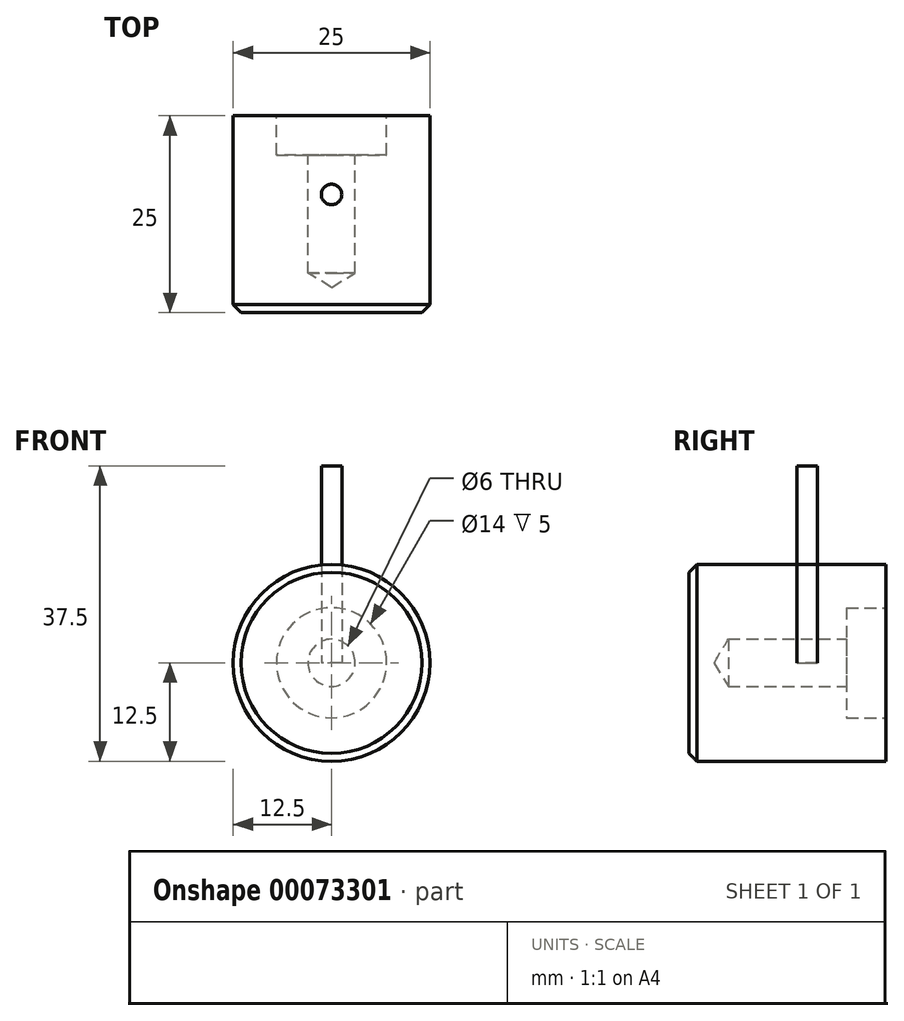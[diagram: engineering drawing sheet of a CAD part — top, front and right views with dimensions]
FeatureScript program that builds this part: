
annotation { "Feature Type Name" : "Feature", "Feature Type Description" : "" }
export const myFeature = defineFeature(function(context is Context, id is Id, definition is map)
    precondition{}
    {
        {
            var Q0;
            Q0=qCreatedBy(makeId("Front.planeOp"),FACE);
            var sketch = newSketch(context, id + "F0", { "sketchPlane" : qUnion([Q0])});
            skCircle(sketch, "E0", {"center": v(0, 0) * mm, "radius": 12.5 * mm});
            skSolve(sketch);
        }
        {
            var Q0;
            Q0=qSketchRegion(id+"F0",true);
            var Q1;
            Q1=makeQuery(id+"F0.imprint","IMPRINT",FACE,{"disambiguationData":[TD([[makeQuery(id+"F0.imprint","IMPRINT",EDGE,{"derivedFrom":sQuery(id+"F0.wireOp",EDGE,"E0")}),1.0]])]});
            extrude(context, id + "F1", {"entities" : qUnion([Q0, Q1]), "depth" : 25 * mm});
        }
        {
            var Q0;
            Q0=makeQuery(id+"F1.opExtrude","CAP_EDGE",EDGE,{"disambiguationData":[OSD([sQuery(id+"F0.wireOp",EDGE,"E0")])],"isStart":false});
            chamfer(context, id + "F2", {"entities" : qUnion([Q0]), "width" : 1 * mm, "tangentPropagation" : true});
        }
        {
            var Q0;
            Q0=makeQuery(id+"F1.opExtrude","CAP_FACE",FACE,{"disambiguationData":[OSD([sQuery(id+"F0.wireOp",EDGE,"E0")])],"isStart":true});
            var sketch = newSketch(context, id + "F3", { "sketchPlane" : qUnion([Q0])});
            skPoint(sketch, "E1", {"position": v(0, 0) * mm});
            skSolve(sketch);
        }
        {
            var Q0;
            Q0=sQuery(id+"F3.wireOp",VERTEX,"E1");
            var Q1;
            Q1=makeQuery(id+"F1.opExtrude","SWEPT_BODY",BODY,{"disambiguationData":[OSD([sQuery(id+"F0.wireOp",EDGE,"E0")])]});
            hole(context, id + "F4", {"style" : HoleStyle.C_BORE, "holeDiameter" : 6 * mm, "cBoreDiameter" : 14 * mm, "cBoreDepth" : 5 * mm, "endStyle" : HoleEndStyle.BLIND, "holeDepth" : 20 * mm, "locations" : qUnion([Q0]), "scope" : qUnion([Q1])});
        }
        {
            var Q0;
            Q0=qCreatedBy(makeId("Top.planeOp"),FACE);
            var sketch = newSketch(context, id + "F5", { "sketchPlane" : qUnion([Q0])});
            skCircle(sketch, "E2", {"center": v(0, -10) * mm, "radius": 1.3 * mm});
            skSolve(sketch);
        }
        {
            var Q0;
            Q0 = qSketchRegion(id + "F5", true);
            var Q1;
            Q1=sQuery(id+"F5.wireOp",EDGE,"E2");
            extrude(context, id + "F6", {"entities" : qUnion([Q0]), "surfaceEntities" : qUnion([Q1]), "depth" : 25 * mm});
        }
    });
